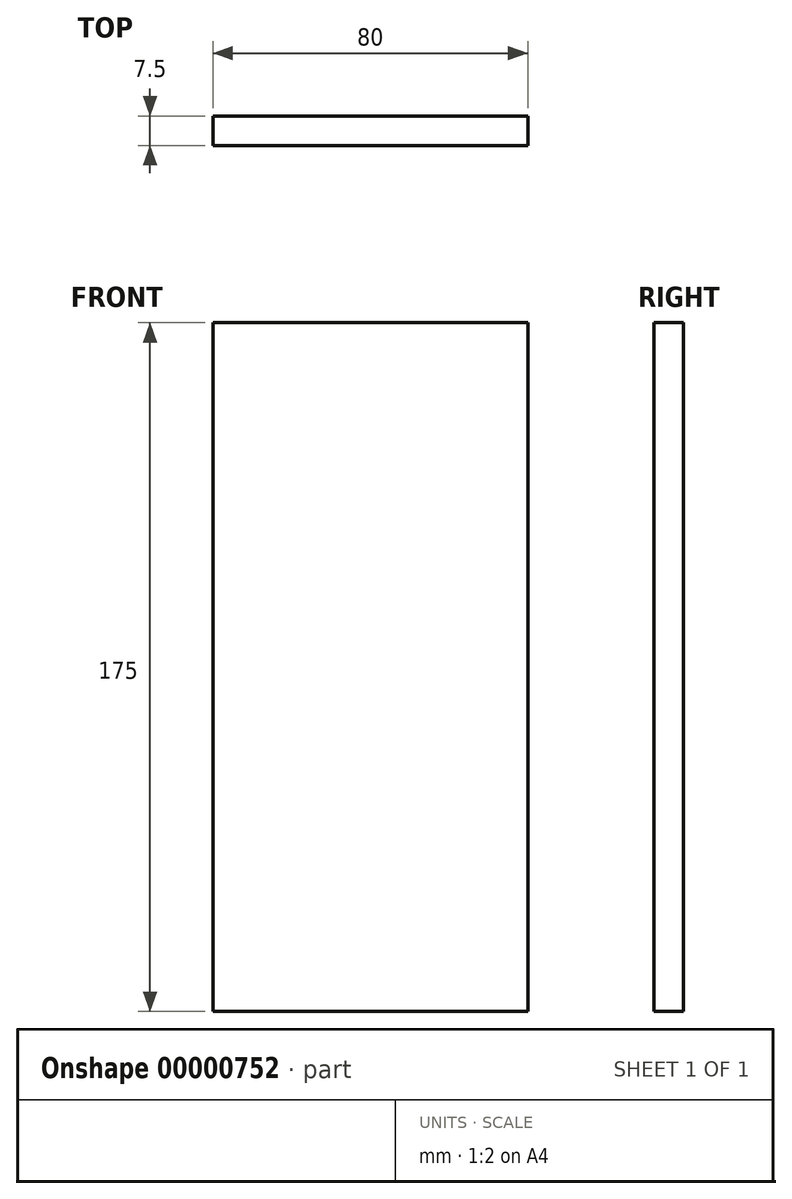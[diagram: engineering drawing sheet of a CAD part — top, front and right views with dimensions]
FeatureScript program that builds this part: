
annotation { "Feature Type Name" : "Feature", "Feature Type Description" : "" }
export const myFeature = defineFeature(function(context is Context, id is Id, definition is map)
    precondition{}
    {
        {
            var Q0;
            Q0=qCreatedBy(makeId("Front.planeOp"),FACE);
            var sketch = newSketch(context, id + "F0", { "sketchPlane" : qUnion([Q0])});
            skLineSegment(sketch, "E0", {"start": v(0, 0) * mm, "end": v(0, 175) * mm});
            skLineSegment(sketch, "E1", {"start": v(0, 175) * mm, "end": v(80, 175) * mm});
            skLineSegment(sketch, "E2", {"start": v(80, 175) * mm, "end": v(80, 0) * mm});
            skLineSegment(sketch, "E3", {"start": v(80, 0) * mm, "end": v(0, 0) * mm});
            skSolve(sketch);
        }
        {
            var Q0;
            Q0=makeQuery(id+"F0.imprint","IMPRINT",FACE,{"disambiguationData":[TD([[makeQuery(id+"F0.imprint","IMPRINT",EDGE,{"derivedFrom":sQuery(id+"F0.wireOp",EDGE,"E0")}),-1.0]])]});
            extrude(context, id + "F1", {"entities" : qUnion([Q0]), "depth" : 7.5 * mm});
        }
    });
